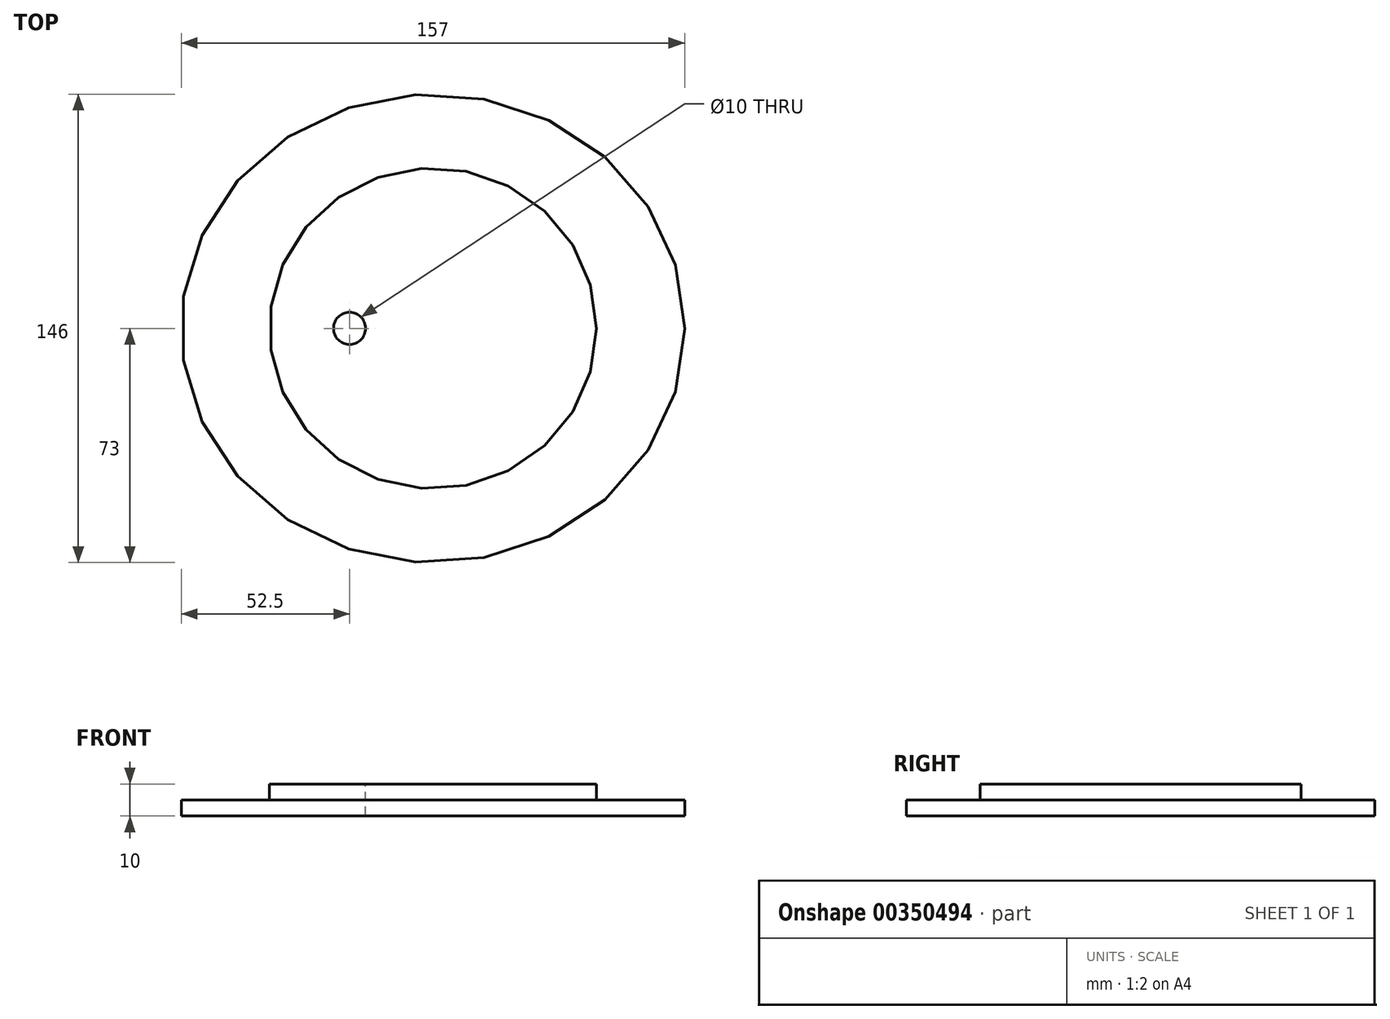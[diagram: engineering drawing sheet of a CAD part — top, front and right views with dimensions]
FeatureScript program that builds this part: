
annotation { "Feature Type Name" : "Feature", "Feature Type Description" : "" }
export const myFeature = defineFeature(function(context is Context, id is Id, definition is map)
    precondition{}
    {
        {
            var Q0;
            Q0=qCreatedBy(makeId("Top.planeOp"),FACE);
            var sketch = newSketch(context, id + "F0", { "sketchPlane" : qUnion([Q0])});
            skEllipse(sketch, "E0", {"center": v(0, 0) * mm, "majorRadius": 78.5 * mm, "minorRadius": 73 * mm, "majorAxis": v(1, 0)});
            skSolve(sketch);
        }
        {
            var Q0;
            Q0=makeQuery(id+"F0.imprint","IMPRINT",FACE,{"disambiguationData":[TD([[makeQuery(id+"F0.imprint","IMPRINT",EDGE,{"derivedFrom":sQuery(id+"F0.wireOp",EDGE,"E0")}),1.0]])]});
            extrude(context, id + "F1", {"entities" : qUnion([Q0]), "depth" : 5 * mm});
        }
        {
            var Q0;
            Q0=makeQuery(id+"F1.opExtrude","CAP_FACE",FACE,{"disambiguationData":[OSD([sQuery(id+"F0.wireOp",EDGE,"E0")])],"isStart":false});
            var sketch = newSketch(context, id + "F2", { "sketchPlane" : qUnion([Q0])});
            skEllipse(sketch, "E1", {"center": v(0, 0) * mm, "majorRadius": 51 * mm, "minorRadius": 50 * mm, "majorAxis": v(1, 0)});
            skSolve(sketch);
        }
        {
            var Q0;
            Q0=makeQuery(id+"F2.imprint","IMPRINT",FACE,{"disambiguationData":[TD([[makeQuery(id+"F2.imprint","IMPRINT",EDGE,{"derivedFrom":sQuery(id+"F2.wireOp",EDGE,"E1")}),1.0]])]});
            var Q1;
            Q1=sQuery(id+"F2.wireOp",EDGE,"E1");
            extrude(context, id + "F3", {"entities" : qUnion([Q0]), "operationType" : NewBodyOperationType.ADD, "surfaceEntities" : qUnion([Q1]), "depth" : 5 * mm});
        }
        {
            var Q0;
            Q0=makeQuery(id+"F3.opExtrude","CAP_FACE",FACE,{"disambiguationData":[OSD([sQuery(id+"F2.wireOp",EDGE,"E1")])],"isStart":false});
            var sketch = newSketch(context, id + "F4", { "sketchPlane" : qUnion([Q0])});
            skCircle(sketch, "E2", {"center": v(-26, 0) * mm, "radius": 5 * mm});
            skLineSegment(sketch, "E3", {"start": v(-26, 0) * mm, "end": v(-51, 0) * mm, "construction": true});
            skSolve(sketch);
        }
        {
            var Q0;
            Q0=makeQuery(id+"F4.imprint","IMPRINT",FACE,{"disambiguationData":[TD([[makeQuery(id+"F4.imprint","IMPRINT",EDGE,{"derivedFrom":sQuery(id+"F4.wireOp",EDGE,"E2")}),1.0]])]});
            extrude(context, id + "F5", {"entities" : qUnion([Q0]), "operationType" : NewBodyOperationType.REMOVE, "endBound" : BoundingType.THROUGH_ALL, "oppositeDirection" : true, "depth" : 25 * mm});
        }
    });
